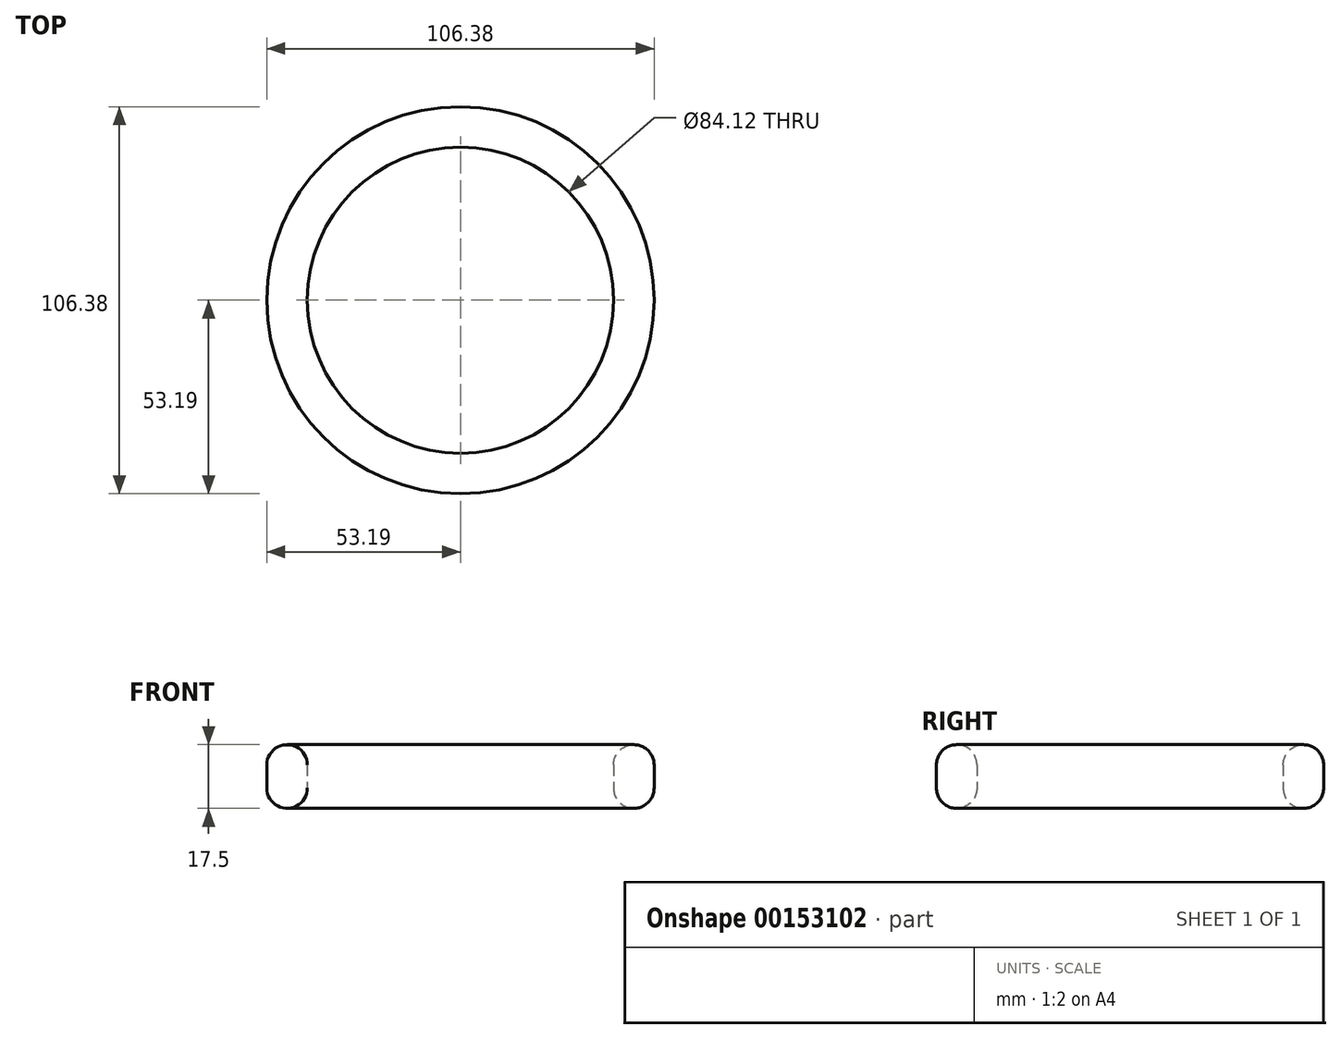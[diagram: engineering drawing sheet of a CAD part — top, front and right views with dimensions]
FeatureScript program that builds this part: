
annotation { "Feature Type Name" : "Feature", "Feature Type Description" : "" }
export const myFeature = defineFeature(function(context is Context, id is Id, definition is map)
    precondition{}
    {
        {
            var Q0;
            Q0=qCreatedBy(makeId("Front.planeOp"),FACE);
            var sketch = newSketch(context, id + "F0", { "sketchPlane" : qUnion([Q0])});
            skLineSegment(sketch, "E0", {"start": v(0, 0) * mm, "end": v(0, 41.99) * mm, "construction": true});
            skLineSegment(sketch, "E1.bottom", {"start": v(47.62, 13.8) * mm, "end": v(47.62, 13.8) * mm});
            skLineSegment(sketch, "E1.top", {"start": v(47.62, -3.7) * mm, "end": v(47.62, -3.7) * mm});
            skLineSegment(sketch, "E1.left", {"start": v(42.06, 8.24) * mm, "end": v(42.06, 1.87) * mm});
            skLineSegment(sketch, "E1.right", {"start": v(53.19, 8.24) * mm, "end": v(53.19, 1.87) * mm});
            skPoint(sketch, "E2.visualSharp", {"position": v(42.06, 13.8) * mm});
            skArc(sketch, "E2.filletArc", {"start": v(47.62, 13.8) * mm, "mid": v(43.69, 12.17) * mm, "end": v(42.06, 8.24) * mm});
            skPoint(sketch, "E3.visualSharp", {"position": v(53.19, 13.8) * mm});
            skArc(sketch, "E3.filletArc", {"start": v(53.19, 8.24) * mm, "mid": v(51.56, 12.17) * mm, "end": v(47.62, 13.8) * mm});
            skPoint(sketch, "E4.visualSharp", {"position": v(53.19, -3.7) * mm});
            skArc(sketch, "E4.filletArc", {"start": v(47.62, -3.7) * mm, "mid": v(51.56, -2.07) * mm, "end": v(53.19, 1.87) * mm});
            skPoint(sketch, "E5.visualSharp", {"position": v(42.06, -3.7) * mm});
            skArc(sketch, "E5.filletArc", {"start": v(42.06, 1.87) * mm, "mid": v(43.69, -2.07) * mm, "end": v(47.62, -3.7) * mm});
            skSolve(sketch);
        }
        {
            var Q0;
            Q0=makeQuery(id+"F0.imprint","IMPRINT",FACE,{"disambiguationData":[TD([[makeQuery(id+"F0.imprint","IMPRINT",EDGE,{"derivedFrom":sQuery(id+"F0.wireOp",EDGE,"E1.left")}),1.0]])]});
            var Q1;
            Q1=sQuery(id+"F0.wireOp",EDGE,"E0");
            revolve(context, id + "F1", {"entities" : qUnion([Q0]), "axis" : qUnion([Q1]), "revolveType" : RevolveType.FULL});
        }
    });
